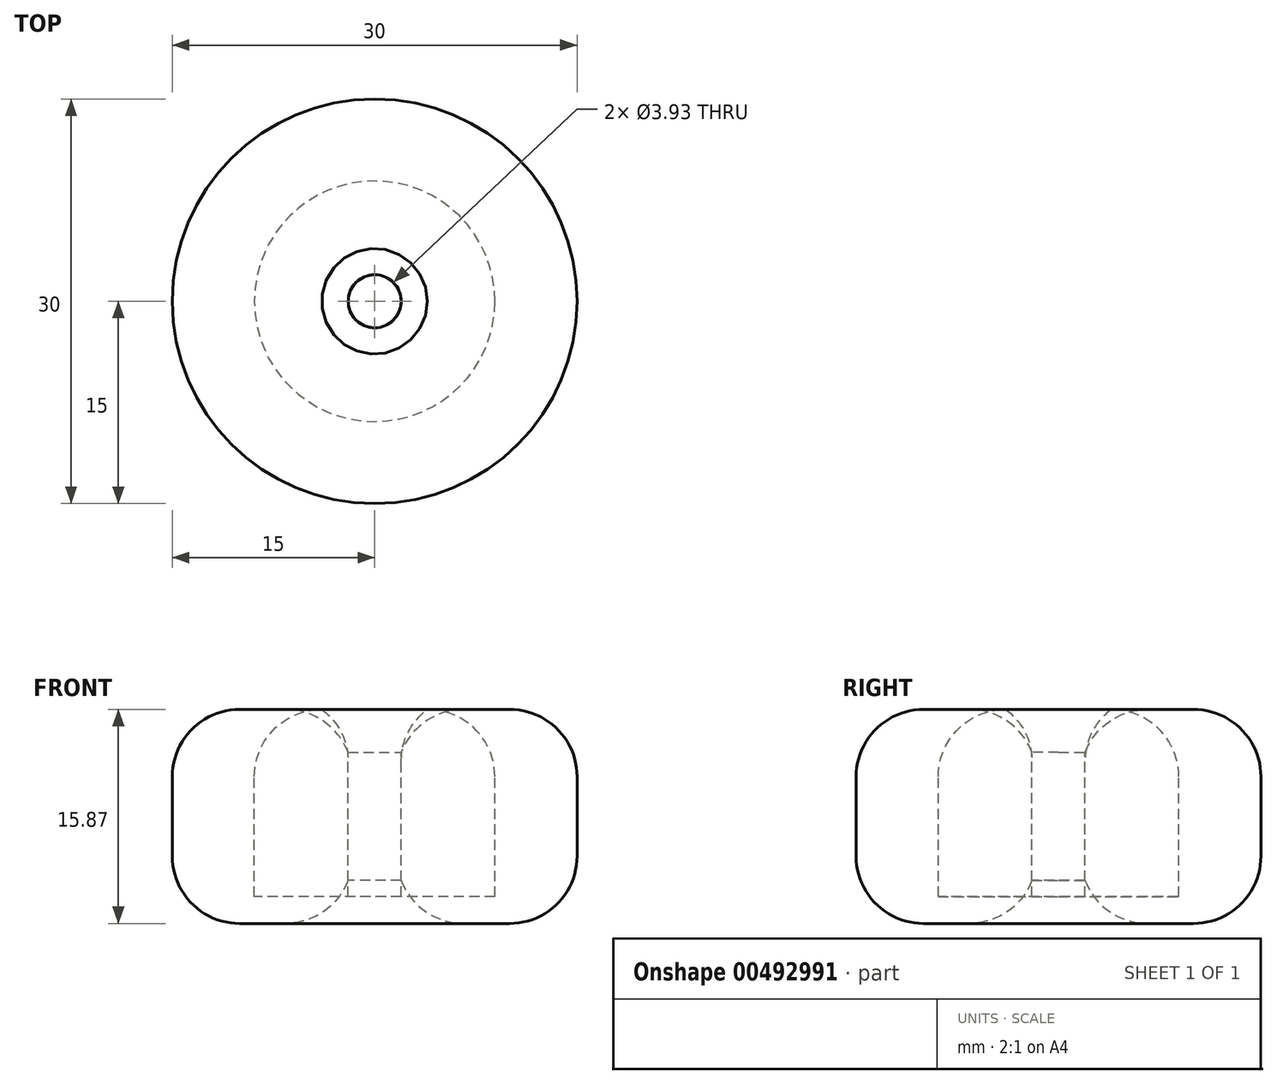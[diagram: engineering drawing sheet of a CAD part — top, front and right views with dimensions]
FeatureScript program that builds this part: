
annotation { "Feature Type Name" : "Feature", "Feature Type Description" : "" }
export const myFeature = defineFeature(function(context is Context, id is Id, definition is map)
    precondition{}
    {
        {
            var Q0;
            Q0=qCreatedBy(makeId("Top.planeOp"),FACE);
            var sketch = newSketch(context, id + "F0", { "sketchPlane" : qUnion([Q0])});
            skCircle(sketch, "E0", {"center": v(0, 0) * mm, "radius": 15 * mm});
            skSolve(sketch);
        }
        {
            var Q0;
            Q0=makeQuery(id+"F0.imprint","IMPRINT",FACE,{"disambiguationData":[TD([[makeQuery(id+"F0.imprint","IMPRINT",EDGE,{"derivedFrom":sQuery(id+"F0.wireOp",EDGE,"E0")}),1.0]])]});
            extrude(context, id + "F1", {"entities" : qUnion([Q0]), "oppositeDirection" : true, "depth" : 15.88 * mm, "offsetDistance" : 25 * mm});
        }
        {
            var Q0;
            Q0=qCreatedBy(makeId("Top.planeOp"),FACE);
            var sketch = newSketch(context, id + "F2", { "sketchPlane" : qUnion([Q0])});
            skCircle(sketch, "E1", {"center": v(0, 0) * mm, "radius": 1.63 * mm});
            skSolve(sketch);
        }
        {
            var Q0;
            Q0 = qSketchRegion(id + "F2", true);
            extrude(context, id + "F3", {"entities" : qUnion([Q0]), "operationType" : NewBodyOperationType.REMOVE, "oppositeDirection" : true, "depth" : 15.88 * mm, "offsetDistance" : 25 * mm});
        }
        {
            var Q0;
            Q0=qCreatedBy(makeId("Top.planeOp"),FACE);
            var sketch = newSketch(context, id + "F4", { "sketchPlane" : qUnion([Q0])});
            skCircle(sketch, "E2", {"center": v(0, 0) * mm, "radius": 8.91 * mm});
            skSolve(sketch);
        }
        {
            var Q0;
            Q0=makeQuery(id+"F4.imprint","IMPRINT",FACE,{"disambiguationData":[TD([[makeQuery(id+"F4.imprint","IMPRINT",EDGE,{"derivedFrom":sQuery(id+"F4.wireOp",EDGE,"E2")}),1.0]])]});
            extrude(context, id + "F5", {"entities" : qUnion([Q0]), "oppositeDirection" : true, "depth" : 13.88 * mm, "offsetDistance" : 25.4 * mm});
        }
        {
            var Q0;
            Q0=makeQuery(id+"F1.opExtrude","CAP_FACE",FACE,{"disambiguationData":[OSD([sQuery(id+"F0.wireOp",EDGE,"E0")])],"isStart":true});
            var Q1;
            Q1=makeQuery(id+"F5.opExtrude","CAP_FACE",FACE,{"disambiguationData":[OSD([sQuery(id+"F4.wireOp",EDGE,"E2")])],"isStart":true});
            fillet(context, id + "F6", {"entities" : qUnion([Q0, Q1]), "radius" : 5 * mm, "tangentPropagation" : true, "allowEdgeOverflow" : false});
        }
        {
            var Q0;
            Q0=makeQuery(id+"F1.opExtrude","CAP_FACE",FACE,{"disambiguationData":[OSD([sQuery(id+"F0.wireOp",EDGE,"E0")])],"isStart":false});
            var Q1;
            Q1=makeQuery(id+"F5.opExtrude","CAP_FACE",FACE,{"disambiguationData":[OSD([sQuery(id+"F4.wireOp",EDGE,"E2")])],"isStart":true});
            fillet(context, id + "F7", {"entities" : qUnion([Q0, Q1]), "radius" : 5 * mm, "tangentPropagation" : true, "allowEdgeOverflow" : false});
        }
        {
            var Q0;
            Q0=qCreatedBy(makeId("Top.planeOp"),FACE);
            var sketch = newSketch(context, id + "F8", { "sketchPlane" : qUnion([Q0])});
            skCircle(sketch, "E3", {"center": v(0, 0) * mm, "radius": 1.97 * mm});
            skSolve(sketch);
        }
        {
            var Q0;
            Q0 = qSketchRegion(id + "F8", true);
            extrude(context, id + "F9", {"entities" : qUnion([Q0]), "operationType" : NewBodyOperationType.REMOVE, "oppositeDirection" : true, "depth" : 15.88 * mm, "offsetDistance" : 25 * mm});
        }
        {
            var Q0;
            Q0=makeQuery(id+"F5.opExtrude","CAP_FACE",FACE,{"disambiguationData":[OSD([sQuery(id+"F4.wireOp",EDGE,"E2")])],"isStart":true});
            fillet(context, id + "F10", {"entities" : qUnion([Q0]), "radius" : 5 * mm, "rho" : 0.5, "crossSection" : FilletCrossSection.CONIC, "allowEdgeOverflow" : false});
        }
        {
            var Q0;
            Q0=qCreatedBy(makeId("Front.planeOp"),FACE);
            var sketch = newSketch(context, id + "F11", { "sketchPlane" : qUnion([Q0])});
            skLineSegment(sketch, "E4", {"start": v(0, 0) * mm, "end": v(0, -8.08) * mm});
            skSolve(sketch);
        }
        {
            var Q0;
            Q0=makeQuery(id+"F1.opExtrude","SWEPT_BODY",BODY,{"disambiguationData":[OSD([sQuery(id+"F0.wireOp",EDGE,"E0")])]});
            var Q1;
            Q1=makeQuery(id+"F5.opExtrude","SWEPT_BODY",BODY,{"disambiguationData":[OSD([sQuery(id+"F4.wireOp",EDGE,"E2")])]});
            var Q2;
            Q2=sQuery(id+"F11.wireOp",EDGE,"E4");
            transform(context, id + "F12", {"entities" : qUnion([Q0, Q1]), "transformType" : TransformType.TRANSLATION_ENTITY, "oppositeDirectionEntity" : true, "transformLine" : qUnion([Q2]), "makeCopy" : false});
        }
    });
